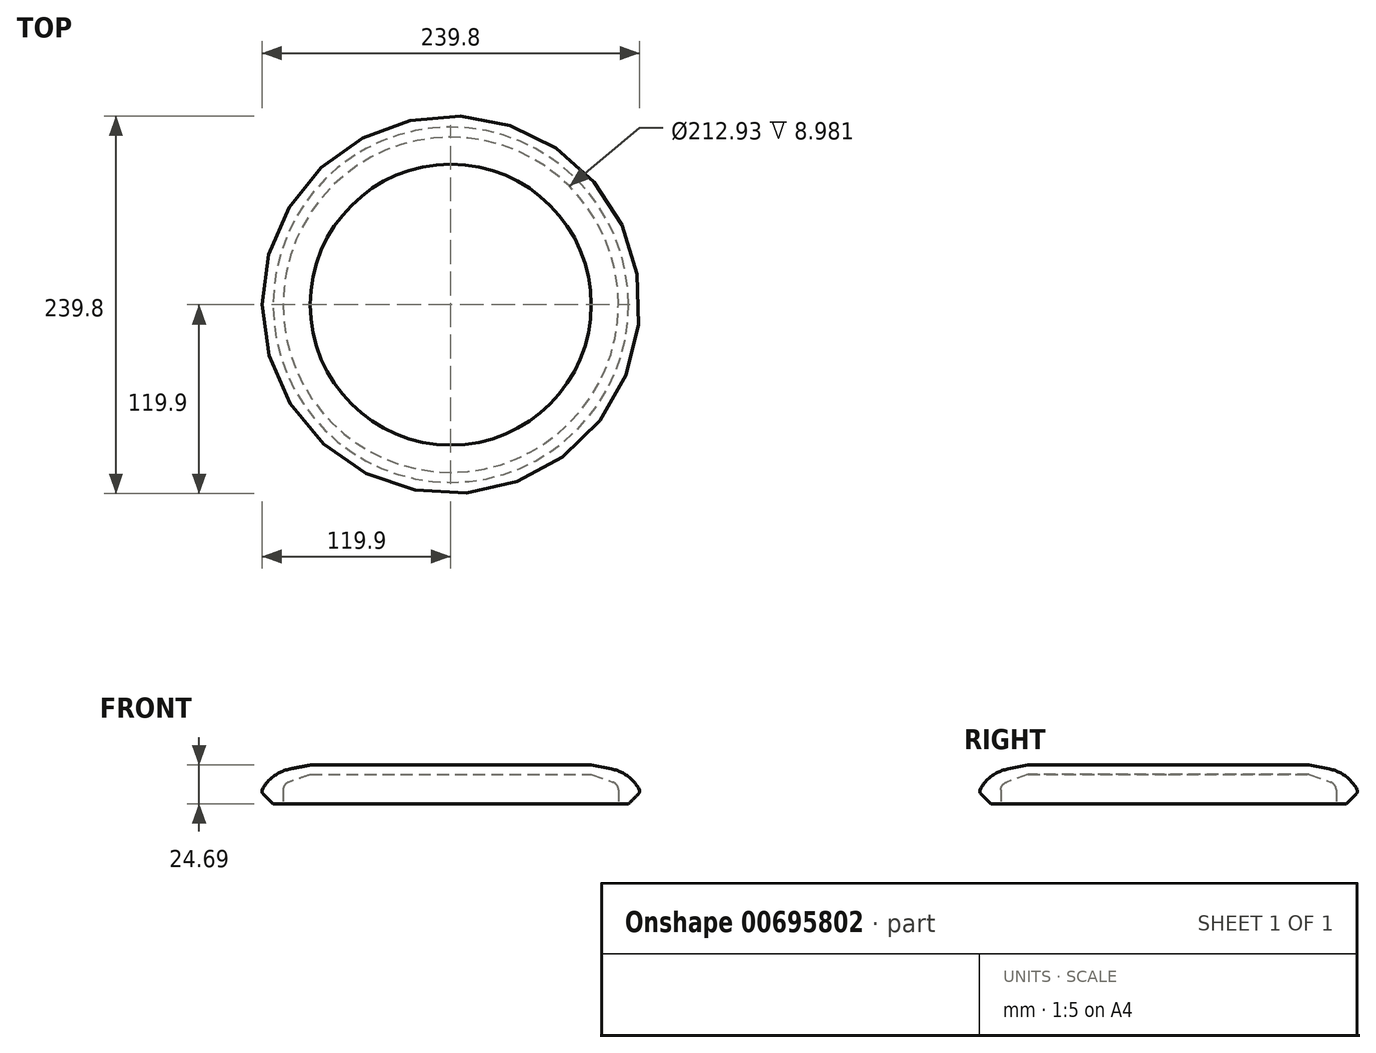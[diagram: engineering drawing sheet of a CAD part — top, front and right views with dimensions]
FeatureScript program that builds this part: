
annotation { "Feature Type Name" : "Feature", "Feature Type Description" : "" }
export const myFeature = defineFeature(function(context is Context, id is Id, definition is map)
    precondition{}
    {
        {
            var Q0;
            Q0=qCreatedBy(makeId("Front.planeOp"),FACE);
            var sketch = newSketch(context, id + "F0", { "sketchPlane" : qUnion([Q0])});
            skLineSegment(sketch, "E0", {"start": v(0, 28.65) * mm, "end": v(89.23, 28.65) * mm});
            skLineSegment(sketch, "E1", {"start": v(89.23, 28.65) * mm, "end": v(120.44, 22.6) * mm});
            skLineSegment(sketch, "E2", {"start": v(120.44, 22.6) * mm, "end": v(120.44, 3.96) * mm});
            skLineSegment(sketch, "E3", {"start": v(120.44, 3.96) * mm, "end": v(106.47, 3.96) * mm});
            skLineSegment(sketch, "E4", {"start": v(106.47, 3.96) * mm, "end": v(106.47, 16.54) * mm});
            skLineSegment(sketch, "E5", {"start": v(106.47, 16.54) * mm, "end": v(89.23, 22.6) * mm});
            skLineSegment(sketch, "E6", {"start": v(89.23, 22.6) * mm, "end": v(0, 22.6) * mm});
            skLineSegment(sketch, "E7", {"start": v(0, 22.6) * mm, "end": v(0, 28.65) * mm});
            skSolve(sketch);
        }
        {
            var Q0;
            Q0=makeQuery(id+"F0.imprint","IMPRINT",FACE,{"disambiguationData":[TD([[makeQuery(id+"F0.imprint","IMPRINT",EDGE,{"derivedFrom":sQuery(id+"F0.wireOp",EDGE,"E0")}),-1.0]])]});
            var Q1;
            Q1=sQuery(id+"F0.wireOp",EDGE,"E7");
            revolve(context, id + "F1", {"entities" : qUnion([Q0]), "axis" : qUnion([Q1]), "revolveType" : RevolveType.FULL});
        }
        {
            var Q0;
            Q0=makeQuery(id+"F1.opRevolve","SWEPT_EDGE",EDGE,{"disambiguationData":[OSD([sQuery(id+"F0.wireOp",EDGE,"E2"),sQuery(id+"F0.wireOp",EDGE,"E3")])]});
            chamfer(context, id + "F2", {"entities" : qUnion([Q0]), "width" : 7.62 * mm, "tangentPropagation" : true});
        }
        {
            var Q0;
            Q0=makeQuery(id+"F1.opRevolve","SWEPT_EDGE",EDGE,{"disambiguationData":[OSD([sQuery(id+"F0.wireOp",EDGE,"E1"),sQuery(id+"F0.wireOp",EDGE,"E2")])]});
            fillet(context, id + "F3", {"entities" : qUnion([Q0]), "radius" : 25.4 * mm, "tangentPropagation" : true, "allowEdgeOverflow" : false});
        }
        {
            var Q0;
            {var subQ0=sQuery(id+"F0.wireOp",EDGE,"E2");Q0=makeQuery(id+"F3.opFillet","BLEND_EDGE",EDGE,{"blendedFrom":[makeQuery(id+"F1.opRevolve","SWEPT_EDGE",EDGE,{"disambiguationData":[OSD([sQuery(id+"F0.wireOp",EDGE,"E1"),subQ0])]}),makeQuery(id+"F2.opChamfer","BLEND_FACE",FACE,{"disambiguationData":[OSD([subQ0,sQuery(id+"F0.wireOp",EDGE,"E3")])]})],"blendedInto":[makeQuery(id+"F2.opChamfer","BLEND_FACE",FACE,{"disambiguationData":[OSD([subQ0,sQuery(id+"F0.wireOp",EDGE,"E3")])]})]});}
            fillet(context, id + "F4", {"entities" : qUnion([Q0]), "radius" : 2.54 * mm, "tangentPropagation" : true, "allowEdgeOverflow" : false});
        }
        {
            var Q0;
            Q0=makeQuery(id+"F1.opRevolve","SWEPT_EDGE",EDGE,{"disambiguationData":[OSD([sQuery(id+"F0.wireOp",EDGE,"E4"),sQuery(id+"F0.wireOp",EDGE,"E5")])]});
            fillet(context, id + "F5", {"entities" : qUnion([Q0]), "radius" : 5.08 * mm, "tangentPropagation" : true, "allowEdgeOverflow" : false});
        }
    });
